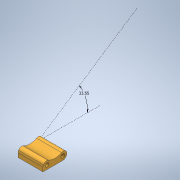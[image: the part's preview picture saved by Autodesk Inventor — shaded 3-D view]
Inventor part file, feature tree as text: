
AUTODESK INVENTOR PART (.ipt)
format: ipt  version: 2020 (Build 240168000, 168)  size: 264,192 bytes
history: native  units: in
note: dims shown in document units (in); Inventor stores cm internally (conversion verified against a paired STEP export)
features: sketch x7, extrude x6, projected_geometry x4, other x3, fillet x2
ambient origin geometry x8: Origin, YZ Plane, XZ Plane, XY Plane, X Axis, Y Axis, Z Axis, Center Point
bodies: Solid1 (feature_tree)
feature tree (22):
  other  "Assembly4.iam"
  other  "Kauri modular session 5 mount.ipt:1"
  other  "session 5.ipt:1"
  extrude  "Extrusion1"  Depth=0.3937in TaperAngle=0.0deg
  extrude  "Extrusion2"  Depth=1.0in TaperAngle=0.0deg
  extrude  "Extrusion3"  Depth=0.3937in TaperAngle=0.0deg
  fillet  "Fillet1"  Radius=0.2362in
  fillet  "Fillet2"  Radius=0.0394in
  extrude  "Extrusion4"  Depth=0.3937in
  extrude  "Extrusion6"  Depth=0.0197in
  sketch  "Sketch7"  dims[d20=0.0197in d23=0.3937in d24=0.0in]
  extrude  "Extrusion7"  Depth=0.3937in TaperAngle=0.0deg
  sketch  "Sketch1"  dims[d0=0.3937in d1=1.0in d2=0.0in]
  projected_geometry  "Projected Loop1"
  sketch  "Sketch2"  dims[d3=0.5906in d4=1.0in d5=0.0in]
  sketch  "Sketch3"  dims[d6=0.9843in d7=0.3937in d8=0.0in d9=0.2362in d10=0.0394in]
  projected_geometry  "Projected Loop2"
  sketch  "Sketch4"  dims[d12=0.0197in d15=0.3937in d16=0.0in d17=0.0197in]
  projected_geometry  "Projected Loop3"
  sketch  "Sketch6"  dims[d18=0.0197in d19=0.0197in]
  sketch  "Sketch8"  dims[d25=0.2305in d26=0.3937in d27=0.0in]
  projected_geometry  "Projected Loop5"
